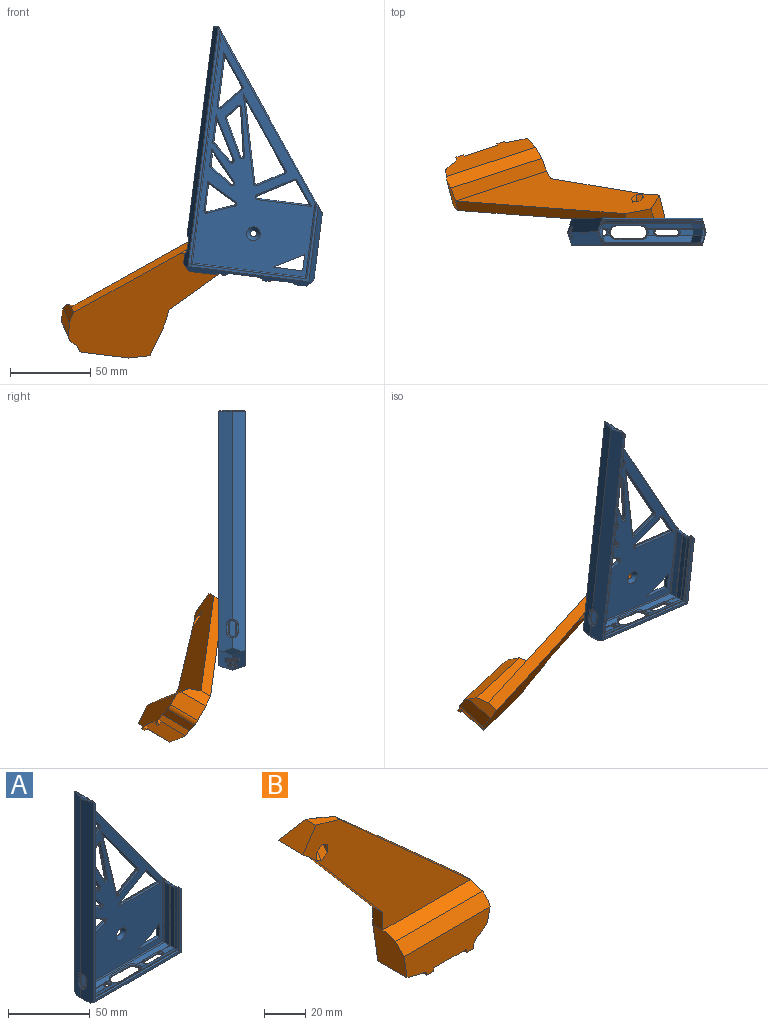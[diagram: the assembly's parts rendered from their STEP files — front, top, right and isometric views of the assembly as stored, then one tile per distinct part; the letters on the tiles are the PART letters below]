
ASSEMBLY  parts=2 mates=1
PART A: 277 faces, bbox 82x17x153.9 mm
  f0: plane 148.63x75.45mm, normal (0,1,0), area 4934.7mm2, adj f16,f37,f50,f70,f81,f82,f83,f110
  f1: cylinder r=0.8mm len=18.94mm, axis (1,0,0), area 5.1mm2, adj f33,f35,f47,f167
  f2: cylinder r=0.8mm len=5.41mm, axis (1,0,0), area 1.4mm2, adj f9,f35,f130,f158
  f3: cylinder r=0.8mm len=5.41mm, axis (1,0,0), area 1.4mm2, adj f9,f31,f134,f154
  f4: cylinder r=0.8mm len=2.64mm, axis (1,0,0), area 0.6mm2, adj f8,f31,f133,f164
  f5: plane 144.41x71.88mm, normal (0,-1,0), area 4754.3mm2, adj f17,f36,f49,f65,f81,f82,f83,f113
  f6: plane 13.8x13.8mm, normal (0,1,0), area 137mm2, adj f64,f69
  f7: cylinder r=0.8mm len=9.41mm, axis (1,0,0), area 2.5mm2, adj f10,f21,f31,f153
  f8: plane 3.72x1.63mm, normal (0,0,1), area 3.2mm2, adj f4,f34,f131,f162
  f9: plane 4.48x3.72mm, normal (0,0,1), area 13.9mm2, adj f2,f3,f132,f156
  f10: plane 8.76x3.72mm, normal (0,0,1), area 30.8mm2, adj f7,f11,f20,f155
  f11: cylinder r=0.8mm len=9.41mm, axis (1,0,0), area 2.5mm2, adj f10,f19,f35,f157
  f12: cylinder r=0.8mm len=132.11mm, axis (0,0,-1), area 36.6mm2, adj f13,f44,f99,f145
  f13: plane 131.79x3.73mm, normal (1,0,0), area 488.7mm2, adj f12,f14,f15,f99,f107,f143
  f14: cylinder r=0.8mm len=132.11mm, axis (0,0,-1), area 36.6mm2, adj f13,f48,f107,f141
  f15: plane 11.74x2.24mm, normal (0,0,1), area 11.7mm2, adj f13,f71,f73,f99,f100,f106,f107,f108
  f16: plane 47.9x8.81mm, normal (0.94,0.34,0), area 412.5mm2, adj f0,f26,f37,f74,f110,f112
  f17: cylinder r=0.8mm len=47.24mm, axis (0,0,1), area 44.9mm2, adj f5,f18,f36,f115
  f18: plane 46.45x3.49mm, normal (-0.94,-0.34,0), area 166.9mm2, adj f17,f19,f35,f117
  f19: cylinder r=0.8mm len=44.78mm, axis (0,0,1), area 12.4mm2, adj f11,f18,f20,f119
  f20: plane 44.65x3.72mm, normal (-1,0,0), area 166.1mm2, adj f10,f19,f21,f121
  f21: cylinder r=0.8mm len=44.78mm, axis (0,0,1), area 12.4mm2, adj f7,f20,f22,f123
  f22: plane 46.71x4.02mm, normal (-0.94,0.34,0), area 192.3mm2, adj f21,f31,f43,f125
  f23: cylinder r=0.8mm len=46.36mm, axis (0,0,1), area 57.8mm2, adj f24,f30,f43,f122
  f24: plane 45.56x0.4mm, normal (-1,0,0), area 18.2mm2, adj f23,f25,f29,f120
  f25: cylinder r=0.8mm len=46.36mm, axis (0,0,1), area 57.8mm2, adj f24,f28,f39,f118
  f26: plane 47.65x8.31mm, normal (0.94,-0.34,0), area 387.6mm2, adj f16,f27,f39,f74,f114,f116
  f27: plane 77.46x8.15mm, normal (0,-0.34,-0.94), area 469.6mm2, adj f26,f37,f38,f39,f72,f74,f172,f174
  f28: cylinder r=0.8mm len=72.6mm, axis (1,0,0), area 90.2mm2, adj f25,f29,f39,f40
  f29: plane 71x0.4mm, normal (0,0,1), area 28.4mm2, adj f24,f28,f30,f41
  f30: cylinder r=0.8mm len=72.6mm, axis (1,0,0), area 90.2mm2, adj f23,f29,f42,f43
  f31: plane 75.9x4.02mm, normal (0,0.34,0.94), area 258.9mm2, adj f3,f4,f7,f22,f32,f43,f44,f135
  f32: cylinder r=0.8mm len=18.94mm, axis (1,0,0), area 5.1mm2, adj f31,f33,f45,f168
  f33: plane 18.21x3.72mm, normal (0,0,1), area 65.8mm2, adj f1,f32,f46,f169
  f34: cylinder r=0.8mm len=2.64mm, axis (1,0,0), area 0.6mm2, adj f8,f35,f129,f163
  f35: plane 75.9x3.49mm, normal (0,-0.34,0.94), area 217.8mm2, adj f1,f2,f11,f18,f34,f36,f48,f126
  f36: cylinder r=0.8mm len=73.38mm, axis (1,0,0), area 71.1mm2, adj f5,f17,f35,f49
  f37: plane 77.46x8.65mm, normal (0,0.34,-0.94), area 509.8mm2, adj f0,f16,f27,f50,f72,f74,f170,f171
  f38: plane 150.44x8.16mm, normal (-0.94,-0.34,0), area 1256.9mm2, adj f27,f39,f50,f72,f105,f106,f184,f186
  f39: plane 149.05x75.81mm, normal (0,-1,0), area 428.9mm2, adj f25,f26,f27,f28,f38,f40,f105,f116
  f40: cylinder r=0.8mm len=145.26mm, axis (0,0,-1), area 182mm2, adj f28,f39,f41,f104
  f41: plane 144.46x0.4mm, normal (1,0,0), area 57.8mm2, adj f29,f40,f42,f103
  f42: cylinder r=0.8mm len=145.26mm, axis (0,0,-1), area 182mm2, adj f30,f41,f43,f102
  f43: plane 145.82x73.38mm, normal (0,1,0), area 53mm2, adj f22,f23,f30,f31,f42,f44,f101,f124
  f44: plane 150.36x4.46mm, normal (0.94,0.34,0), area 626.7mm2, adj f12,f31,f43,f45,f100,f101,f147,f148
  f45: cylinder r=0.8mm len=8.74mm, axis (0,0,-1), area 2.4mm2, adj f32,f44,f46,f146
  f46: plane 8.27x3.72mm, normal (1,0,0), area 29.3mm2, adj f33,f45,f47,f144
  f47: cylinder r=0.8mm len=8.74mm, axis (0,0,-1), area 2.4mm2, adj f1,f46,f48,f142
  f48: plane 150.19x3.49mm, normal (0.94,-0.34,0), area 544.1mm2, adj f14,f35,f47,f49,f109,f138,f139,f140
  f49: cylinder r=0.8mm len=147.21mm, axis (0,0,-1), area 142.8mm2, adj f5,f36,f48,f111
  f50: plane 150.44x8.66mm, normal (-0.94,0.34,0), area 1336.4mm2, adj f0,f37,f38,f72,f108,f110,f182,f183
  f51: plane 5x0.43mm, normal (0,-1,0), area 2.1mm2, adj f52,f54,f138,f183
  f52: cylinder r=2.5mm len=5mm, axis (1,0,0), area 4.5mm2, adj f51,f53,f139,f141,f143,f145,f147,f182
  f53: plane 5x0.43mm, normal (0,1,0), area 2.1mm2, adj f52,f54,f149,f186
  f54: cylinder r=2.5mm len=5mm, axis (1,0,0), area 4.5mm2, adj f51,f53,f140,f142,f144,f146,f148,f185
  f55: plane 11x0.43mm, normal (0,1,0), area 4.7mm2, adj f56,f58,f150,f180
  f56: cylinder r=2mm len=4mm, axis (0,0,1), area 3.9mm2, adj f55,f57,f151,f153,f155,f157,f159,f179
  f57: plane 11x0.43mm, normal (0,-1,0), area 4.7mm2, adj f56,f58,f161,f177
  f58: cylinder r=2mm len=4mm, axis (0,0,1), area 3.9mm2, adj f55,f57,f152,f154,f156,f158,f160,f176
  f59: plane 15x0.43mm, normal (0,1,0), area 6.4mm2, adj f60,f62,f137,f174
  f60: cylinder r=4mm len=8mm, axis (0,0,1), area 5.7mm2, adj f59,f61,f128,f130,f132,f134,f136,f173
  f61: plane 15x0.43mm, normal (0,-1,0), area 6.4mm2, adj f60,f62,f126,f171
  f62: cylinder r=4mm len=8mm, axis (0,0,1), area 5.7mm2, adj f59,f61,f127,f129,f131,f133,f135,f170
  f63: cylinder r=1.89mm len=3.78mm, axis (0,0,1), area 7.3mm2, adj f162,f163,f164,f165,f166,f167,f168,f169
  f64: cylinder r=2mm len=4mm, axis (0,1,0), area 2.5mm2, adj f6,f65
  f65: cone r=2mm half-angle=45deg, axis (0,-1,0), area 64.4mm2, adj f5,f64
  f66: cylinder r=7.4mm len=14.8mm, axis (0,1,0), area 46.5mm2, adj f68,f69
  f67: cylinder r=10.1mm len=20.2mm, axis (0,1,0), area 63.5mm2, adj f68,f70
  f68: plane 20.2x20.2mm, normal (0,1,0), area 148.4mm2, adj f66,f67
  f69: cone r=6.9mm half-angle=45deg, axis (0,-1,0), area 31.8mm2, adj f6,f66
  f70: cone r=10.1mm half-angle=45deg, axis (0,1,0), area 46mm2, adj f0,f67
  f71: plane 107.12x78.66mm, normal (0.81,0,0.59), area 134.7mm2, adj f15,f108,f109,f110,f111,f112,f113,f114
  f72: plane 11.74x4.24mm, normal (-0.71,0,-0.71), area 35.2mm2, adj f27,f37,f38,f50
  f73: plane 4.6x3.15mm, normal (0.81,0,0.59), area 6.6mm2, adj f15,f100,f101,f103,f105,f106
  f74: plane 11.74x4.24mm, normal (0.71,0,-0.71), area 35.2mm2, adj f16,f26,f27,f37
  f75: plane 31.09x0.9mm, normal (1,0,0), area 28mm2, adj f76,f265,f270,f274
  f76: plane 17.75x13.03mm, normal (-0.81,0,-0.59), area 19.8mm2, adj f75,f263,f267,f272
  f77: plane 12.86x11.59mm, normal (-0.74,0,0.67), area 15.6mm2, adj f266,f267,f270,f271
  f78: plane 16.84x0.9mm, normal (1,0,0), area 15.2mm2, adj f79,f252,f257,f262
  f79: plane 17.72x9.78mm, normal (-0.48,0,-0.88), area 18.2mm2, adj f78,f251,f256,f261
  f80: plane 16.54x6.36mm, normal (-0.36,0,0.93), area 15.9mm2, adj f253,f256,f257,f258
  f81: plane 10.14x2.5mm, normal (-1,0,0), area 25.3mm2, adj f0,f5,f82,f83
  f82: plane 18.35x2.5mm, normal (0,0,1), area 45.9mm2, adj f0,f5,f81,f83
  f83: plane 18.39x10.14mm, normal (0.48,0,-0.88), area 52.5mm2, adj f0,f5,f81,f82
  f84: plane 13.72x10.07mm, normal (-0.81,0,-0.59), area 15.3mm2, adj f85,f241,f246,f250
  f85: plane 32.4x0.9mm, normal (0,0,1), area 29.2mm2, adj f84,f239,f243,f248
  f86: plane 21.69x12.45mm, normal (0.5,0,-0.87), area 22.5mm2, adj f242,f243,f246,f247
  f87: plane 22.6x11.63mm, normal (0.89,0,0.46), area 22.9mm2, adj f226,f233,f234,f238
  f88: plane 6.86x6.17mm, normal (0.74,0,-0.67), area 8.3mm2, adj f225,f228,f232,f233
  f89: plane 29.46x5.46mm, normal (-0.98,0,-0.18), area 27mm2, adj f227,f228,f234,f235
  f90: plane 14.08x0.9mm, normal (1,0,0), area 12.7mm2, adj f91,f213,f218,f223
  f91: plane 23.83x13.13mm, normal (-0.88,0,-0.48), area 24.5mm2, adj f90,f212,f217,f222
  f92: plane 11.63x10.13mm, normal (0.66,0,0.75), area 13.9mm2, adj f214,f217,f218,f219
  f93: plane 8.38x0.9mm, normal (1,0,0), area 7.5mm2, adj f94,f201,f206,f211
  f94: plane 17.3x15.12mm, normal (-0.75,0,-0.66), area 20.7mm2, adj f93,f200,f205,f210
  f95: plane 13.72x9.45mm, normal (0.57,0,0.82), area 15mm2, adj f202,f205,f206,f207
  f96: plane 50.74x12.4mm, normal (0.97,0,0.24), area 47mm2, adj f97,f190,f195,f199
  f97: plane 40.81x29.96mm, normal (-0.81,0,-0.59), area 45.6mm2, adj f96,f188,f192,f197
  f98: plane 16.13x9.26mm, normal (-0.5,0,0.87), area 16.7mm2, adj f191,f192,f195,f196
  f99: bspline ~1.16x0.68mm, area 0.1mm2, adj f12,f13,f15,f100
  f100: cylinder r=0.8mm len=4.82mm, axis (0.31,-0.85,-0.42), area 2.9mm2, adj f15,f44,f73,f99,f101
  f101: cylinder r=0.8mm len=1.51mm, axis (0.59,0,-0.81), area 1.1mm2, adj f43,f44,f73,f100,f102
  f102: sphere r=0.8mm, area 0.6mm2, adj f42,f101,f103
  f103: cylinder r=0.8mm len=0.47mm, axis (0,-1,0), area 0.2mm2, adj f41,f73,f102,f104
  f104: sphere r=0.8mm, area 0.6mm2, adj f40,f103,f105
  f105: cylinder r=0.8mm len=3.41mm, axis (-0.59,0,0.81), area 4.1mm2, adj f38,f39,f73,f104,f106
  f106: cylinder r=0.8mm len=8.36mm, axis (-0.34,0.94,0), area 9.7mm2, adj f15,f38,f73,f105,f108
  f107: bspline ~1.16x0.68mm, area 0.1mm2, adj f13,f14,f15,f109
  f108: cylinder r=0.8mm len=8.79mm, axis (0.34,0.94,0), area 10mm2, adj f15,f50,f71,f106,f110
  f109: cylinder r=0.8mm len=3.76mm, axis (-0.31,-0.85,0.42), area 2.3mm2, adj f15,f48,f71,f107,f111
  f110: cylinder r=0.8mm len=104.16mm, axis (0.59,0,-0.81), area 160.4mm2, adj f0,f16,f50,f71,f108,f112
  f111: bspline ~2.52x1.5mm, area 2.3mm2, adj f49,f71,f109,f113
  f112: cylinder r=0.8mm len=8.64mm, axis (0.31,-0.85,-0.42), area 5.4mm2, adj f16,f71,f110,f114
  f113: cylinder r=0.8mm len=98.39mm, axis (-0.59,0,0.81), area 152.6mm2, adj f5,f71,f111,f115
  f114: cylinder r=0.8mm len=8.14mm, axis (-0.31,-0.85,0.42), area 5.1mm2, adj f26,f71,f112,f116
  f115: bspline ~2.65x2.24mm, area 3.7mm2, adj f17,f71,f113,f117
  f116: cylinder r=0.8mm len=2.66mm, axis (-0.59,0,0.81), area 2.7mm2, adj f26,f39,f71,f114,f118
  f117: cylinder r=0.8mm len=3.91mm, axis (-0.31,0.85,0.42), area 8mm2, adj f18,f71,f115,f119
  f118: sphere r=0.8mm, area 1.3mm2, adj f25,f116,f120
  f119: bspline ~1.52x0.9mm, area 0.5mm2, adj f19,f71,f117,f121
  f120: cylinder r=0.8mm len=1.45mm, axis (0,1,0), area 0.8mm2, adj f24,f71,f118,f122
  f121: cylinder r=0.8mm len=3.72mm, axis (0,1,0), area 7.5mm2, adj f20,f71,f119,f123
  f122: sphere r=0.8mm, area 1.1mm2, adj f23,f120,f124
  f123: bspline ~1.52x0.9mm, area 0.5mm2, adj f21,f71,f121,f125
  f124: cylinder r=0.8mm len=1.51mm, axis (0.59,0,-0.81), area 1.3mm2, adj f43,f71,f122,f125
  f125: cylinder r=0.8mm len=4.96mm, axis (0.31,0.85,-0.42), area 9.7mm2, adj f22,f43,f71,f123,f124
  f126: cylinder r=0.8mm len=15mm, axis (1,0,0), area 14.7mm2, adj f35,f61,f127,f128
  f127: bspline ~4.15x2.57mm, area 4.8mm2, adj f35,f62,f126,f129
  f128: bspline ~4.15x2.57mm, area 4.8mm2, adj f35,f60,f126,f130
  f129: bspline ~1.32x1.09mm, area 0.5mm2, adj f34,f62,f127,f131
  f130: bspline ~1.22x0.96mm, area 0.5mm2, adj f2,f60,f128,f132
  f131: torus R=4.8mm, axis (0,0,1), area 4.3mm2, adj f8,f62,f129,f133
  f132: torus R=4.8mm, axis (0,0,1), area 4.3mm2, adj f9,f60,f130,f134
  f133: bspline ~1.22x0.96mm, area 0.5mm2, adj f4,f62,f131,f135
  f134: bspline ~1.32x1.09mm, area 0.5mm2, adj f3,f60,f132,f136
  f135: bspline ~4.15x2.57mm, area 4.8mm2, adj f31,f62,f133,f137
  f136: bspline ~4.15x2.57mm, area 4.8mm2, adj f31,f60,f134,f137
  f137: cylinder r=0.8mm len=15mm, axis (-1,0,0), area 14.7mm2, adj f31,f59,f135,f136
  f138: cylinder r=0.8mm len=5mm, axis (0,0,-1), area 4.9mm2, adj f48,f51,f139,f140
  f139: bspline ~2.44x1.46mm, area 2.2mm2, adj f48,f52,f138,f141
  f140: bspline ~2.44x1.46mm, area 2.2mm2, adj f48,f54,f138,f142
  f141: bspline ~1.6x1.17mm, area 0.6mm2, adj f14,f52,f139,f143
  f142: bspline ~1.46x0.99mm, area 0.6mm2, adj f47,f54,f140,f144
  f143: torus R=3.3mm, axis (1,0,0), area 4.2mm2, adj f13,f52,f141,f145
  f144: torus R=3.3mm, axis (1,0,0), area 4.2mm2, adj f46,f54,f142,f146
  f145: bspline ~1.6x1.17mm, area 0.6mm2, adj f12,f52,f143,f147
  f146: bspline ~1.6x1.17mm, area 0.6mm2, adj f45,f54,f144,f148
  f147: bspline ~2.44x1.46mm, area 2.2mm2, adj f44,f52,f145,f149
  f148: bspline ~2.44x1.46mm, area 2.2mm2, adj f44,f54,f146,f149
  f149: cylinder r=0.8mm len=5mm, axis (0,0,1), area 4.9mm2, adj f44,f53,f147,f148
  f150: cylinder r=0.8mm len=11mm, axis (-1,0,0), area 10.8mm2, adj f31,f55,f151,f152
  f151: bspline ~1.44x0.9mm, area 1.3mm2, adj f31,f56,f150,f153
  f152: bspline ~1.44x0.9mm, area 1.3mm2, adj f31,f58,f150,f154
  f153: bspline ~1.61x1.12mm, area 0.7mm2, adj f7,f56,f151,f155
  f154: bspline ~1.57x1.11mm, area 0.7mm2, adj f3,f58,f152,f156
  f155: torus R=2.8mm, axis (0,0,1), area 4.2mm2, adj f10,f56,f153,f157
  f156: torus R=2.8mm, axis (0,0,1), area 4.2mm2, adj f9,f58,f154,f158
  f157: bspline ~1.4x0.95mm, area 0.7mm2, adj f11,f56,f155,f159
  f158: bspline ~1.61x1.12mm, area 0.7mm2, adj f2,f58,f156,f160
  f159: bspline ~1.44x0.9mm, area 1.3mm2, adj f35,f56,f157,f161
  f160: bspline ~1.44x0.9mm, area 1.3mm2, adj f35,f58,f158,f161
  f161: cylinder r=0.8mm len=11mm, axis (-1,0,0), area 10.8mm2, adj f35,f57,f159,f160
  f162: torus R=2.69mm, axis (0,0,1), area 4.2mm2, adj f8,f63,f163,f164
  f163: bspline ~1.41x1.06mm, area 0.7mm2, adj f34,f63,f162,f165
  f164: bspline ~1.61x1.11mm, area 0.7mm2, adj f4,f63,f162,f166
  f165: bspline ~2.42x0.86mm, area 2.1mm2, adj f35,f63,f163,f167
  f166: bspline ~2.42x0.86mm, area 2.1mm2, adj f31,f63,f164,f168
  f167: bspline ~1.61x1.11mm, area 0.7mm2, adj f1,f63,f165,f169
  f168: bspline ~1.41x1.06mm, area 0.7mm2, adj f32,f63,f166,f169
  f169: torus R=2.69mm, axis (0,0,1), area 4.2mm2, adj f33,f63,f167,f168
  f170: bspline ~5.3x4.8mm, area 10.1mm2, adj f37,f62,f171,f172
  f171: cylinder r=0.8mm len=15mm, axis (-1,0,0), area 23mm2, adj f37,f61,f170,f173
  f172: bspline ~5.3x4.8mm, area 10.1mm2, adj f27,f62,f170,f174
  f173: bspline ~5.3x4.8mm, area 10.1mm2, adj f37,f60,f171,f175
  f174: cylinder r=0.8mm len=15mm, axis (1,0,0), area 23mm2, adj f27,f59,f172,f175
  f175: bspline ~5.3x4.8mm, area 10.1mm2, adj f27,f60,f173,f174
  f176: bspline ~3.27x2.8mm, area 5.5mm2, adj f37,f58,f177,f178
  f177: cylinder r=0.8mm len=11mm, axis (-1,0,0), area 16.9mm2, adj f37,f57,f176,f179
  f178: bspline ~3.27x2.8mm, area 5.5mm2, adj f27,f58,f176,f180
  f179: bspline ~3.27x2.8mm, area 5.5mm2, adj f37,f56,f177,f181
  f180: cylinder r=0.8mm len=11mm, axis (1,0,0), area 16.9mm2, adj f27,f55,f178,f181
  f181: bspline ~3.27x2.8mm, area 5.5mm2, adj f27,f56,f179,f180
  f182: bspline ~4.01x3.3mm, area 6.7mm2, adj f50,f52,f183,f184
  f183: cylinder r=0.8mm len=5mm, axis (0,0,1), area 7.7mm2, adj f50,f51,f182,f185
  f184: bspline ~4.01x3.3mm, area 6.7mm2, adj f38,f52,f182,f186
  f185: bspline ~4.01x3.3mm, area 6.7mm2, adj f50,f54,f183,f187
  f186: cylinder r=0.8mm len=5mm, axis (0,0,-1), area 7.7mm2, adj f38,f53,f184,f187
  f187: bspline ~4.01x3.3mm, area 6.7mm2, adj f38,f54,f185,f186
  f188: cylinder r=0.8mm len=44.52mm, axis (-0.59,0,0.81), area 65.5mm2, adj f0,f97,f189,f190
  f189: torus R=1.6mm, axis (0,1,0), area 2.3mm2, adj f0,f188,f191,f192
  f190: cylinder r=0.8mm len=54.82mm, axis (0.24,0,-0.97), area 67.5mm2, adj f0,f96,f188,f193
  f191: cylinder r=0.8mm len=16.53mm, axis (0.87,0,0.5), area 23.4mm2, adj f0,f98,f189,f193
  f192: cylinder r=0.8mm len=1.17mm, axis (0,-1,0), area 1.2mm2, adj f97,f98,f189,f194
  f193: torus R=1.6mm, axis (0,1,0), area 2.5mm2, adj f0,f190,f191,f195
  f194: torus R=1.6mm, axis (0,-1,0), area 2.3mm2, adj f5,f192,f196,f197
  f195: cylinder r=0.8mm len=1.18mm, axis (0,-1,0), area 1.3mm2, adj f96,f98,f193,f198
  f196: cylinder r=0.8mm len=16.53mm, axis (-0.87,0,-0.5), area 23.4mm2, adj f5,f98,f194,f198
  f197: cylinder r=0.8mm len=44.52mm, axis (0.59,0,-0.81), area 65.5mm2, adj f5,f97,f194,f199
  f198: torus R=1.6mm, axis (0,-1,0), area 2.5mm2, adj f5,f195,f196,f199
  f199: cylinder r=0.8mm len=54.82mm, axis (-0.24,0,0.97), area 67.5mm2, adj f5,f96,f197,f198
  f200: cylinder r=0.8mm len=19.43mm, axis (-0.66,0,0.75), area 30.2mm2, adj f0,f94,f201,f203
  f201: cylinder r=0.8mm len=10.51mm, axis (0,0,-1), area 11.9mm2, adj f0,f93,f200,f204
  f202: cylinder r=0.8mm len=14.17mm, axis (0.82,0,-0.57), area 20.9mm2, adj f0,f95,f203,f204
  f203: torus R=1.6mm, axis (0,1,0), area 4mm2, adj f0,f200,f202,f205
  f204: torus R=1.6mm, axis (0,1,0), area 1.3mm2, adj f0,f201,f202,f206
  f205: cylinder r=0.8mm len=1.33mm, axis (0,-1,0), area 2.1mm2, adj f94,f95,f203,f208
  f206: cylinder r=0.8mm len=0.9mm, axis (0,-1,0), area 0.7mm2, adj f93,f95,f204,f209
  f207: cylinder r=0.8mm len=14.17mm, axis (-0.82,0,0.57), area 20.9mm2, adj f5,f95,f208,f209
  f208: torus R=1.6mm, axis (0,-1,0), area 4mm2, adj f5,f205,f207,f210
  f209: torus R=1.6mm, axis (0,-1,0), area 1.3mm2, adj f5,f206,f207,f211
  f210: cylinder r=0.8mm len=19.43mm, axis (0.66,0,-0.75), area 30.2mm2, adj f5,f94,f208,f211
  f211: cylinder r=0.8mm len=10.51mm, axis (0,0,1), area 11.9mm2, adj f5,f93,f209,f210
  f212: cylinder r=0.8mm len=26.94mm, axis (-0.48,0,0.88), area 35.6mm2, adj f0,f91,f213,f215
  f213: cylinder r=0.8mm len=17.19mm, axis (0,0,-1), area 19.1mm2, adj f0,f90,f212,f216
  f214: cylinder r=0.8mm len=12.16mm, axis (0.75,0,-0.66), area 19.4mm2, adj f0,f92,f215,f216
  f215: torus R=1.6mm, axis (0,1,0), area 3.8mm2, adj f0,f212,f214,f217
  f216: torus R=1.6mm, axis (0,1,0), area 1.2mm2, adj f0,f213,f214,f218
  f217: cylinder r=0.8mm len=1.33mm, axis (0,-1,0), area 2mm2, adj f91,f92,f215,f220
  f218: cylinder r=0.8mm len=0.9mm, axis (0,-1,0), area 0.6mm2, adj f90,f92,f216,f221
  f219: cylinder r=0.8mm len=12.16mm, axis (-0.75,0,0.66), area 19.4mm2, adj f5,f92,f220,f221
  f220: torus R=1.6mm, axis (0,-1,0), area 3.8mm2, adj f5,f217,f219,f222
  f221: torus R=1.6mm, axis (0,-1,0), area 1.2mm2, adj f5,f218,f219,f223
  f222: cylinder r=0.8mm len=26.94mm, axis (0.48,0,-0.88), area 35.6mm2, adj f5,f91,f220,f223
  f223: cylinder r=0.8mm len=17.19mm, axis (0,0,1), area 19.1mm2, adj f5,f90,f221,f222
  f224: torus R=1.6mm, axis (0,1,0), area 3mm2, adj f0,f225,f227,f228
  f225: cylinder r=0.8mm len=7.39mm, axis (-0.67,0,-0.74), area 11.6mm2, adj f0,f88,f224,f229
  f226: cylinder r=0.8mm len=22.97mm, axis (0.46,0,-0.89), area 31.9mm2, adj f0,f87,f229,f230
  f227: cylinder r=0.8mm len=29.6mm, axis (-0.18,0,0.98), area 37.6mm2, adj f0,f89,f224,f230
  f228: cylinder r=0.8mm len=1.38mm, axis (0,-1,0), area 1.6mm2, adj f88,f89,f224,f231
  f229: torus R=1.6mm, axis (0,1,0), area 1.7mm2, adj f0,f225,f226,f233
  f230: torus R=1.6mm, axis (0,1,0), area 3.9mm2, adj f0,f226,f227,f234
  f231: torus R=1.6mm, axis (0,-1,0), area 3mm2, adj f5,f228,f232,f235
  f232: cylinder r=0.8mm len=7.39mm, axis (0.67,0,0.74), area 11.6mm2, adj f5,f88,f231,f236
  f233: cylinder r=0.8mm len=0.9mm, axis (0,-1,0), area 0.9mm2, adj f87,f88,f229,f236
  f234: cylinder r=0.8mm len=1.51mm, axis (0,-1,0), area 2.1mm2, adj f87,f89,f230,f237
  f235: cylinder r=0.8mm len=29.6mm, axis (0.18,0,-0.98), area 37.6mm2, adj f5,f89,f231,f237
  f236: torus R=1.6mm, axis (0,-1,0), area 1.7mm2, adj f5,f232,f233,f238
  f237: torus R=1.6mm, axis (0,-1,0), area 3.9mm2, adj f5,f234,f235,f238
  f238: cylinder r=0.8mm len=22.97mm, axis (-0.46,0,0.89), area 31.9mm2, adj f5,f87,f236,f237
  f239: cylinder r=0.8mm len=33.98mm, axis (1,0,0), area 41.7mm2, adj f0,f85,f240,f241
  f240: torus R=1.6mm, axis (0,1,0), area 3.6mm2, adj f0,f239,f242,f243
  f241: cylinder r=0.8mm len=15.47mm, axis (-0.59,0,0.81), area 22.4mm2, adj f0,f84,f239,f244
  f242: cylinder r=0.8mm len=22.08mm, axis (-0.87,0,-0.5), area 31.4mm2, adj f0,f86,f240,f244
  f243: cylinder r=0.8mm len=1.49mm, axis (0,-1,0), area 1.9mm2, adj f85,f86,f240,f245
  f244: torus R=1.6mm, axis (0,1,0), area 2mm2, adj f0,f241,f242,f246
  f245: torus R=1.6mm, axis (0,-1,0), area 3.6mm2, adj f5,f243,f247,f248
  f246: cylinder r=0.8mm len=1.04mm, axis (0,-1,0), area 1.1mm2, adj f84,f86,f244,f249
  f247: cylinder r=0.8mm len=22.08mm, axis (0.87,0,0.5), area 31.4mm2, adj f5,f86,f245,f249
  f248: cylinder r=0.8mm len=33.98mm, axis (-1,0,0), area 41.7mm2, adj f5,f85,f245,f250
  f249: torus R=1.6mm, axis (0,-1,0), area 2mm2, adj f5,f246,f247,f250
  f250: cylinder r=0.8mm len=15.47mm, axis (0.59,0,-0.81), area 22.4mm2, adj f5,f84,f248,f249
  f251: cylinder r=0.8mm len=19.3mm, axis (-0.88,0,0.48), area 26.3mm2, adj f0,f79,f252,f254
  f252: cylinder r=0.8mm len=18.19mm, axis (0,0,-1), area 22mm2, adj f0,f78,f251,f255
  f253: cylinder r=0.8mm len=16.82mm, axis (0.93,0,0.36), area 22.3mm2, adj f0,f80,f254,f255
  f254: torus R=1.6mm, axis (0,1,0), area 3.1mm2, adj f0,f251,f253,f256
  f255: torus R=1.6mm, axis (0,1,0), area 2.7mm2, adj f0,f252,f253,f257
  f256: cylinder r=0.8mm len=1.45mm, axis (0,-1,0), area 1.6mm2, adj f79,f80,f254,f259
  f257: cylinder r=0.8mm len=1.09mm, axis (0,-1,0), area 1.4mm2, adj f78,f80,f255,f260
  f258: cylinder r=0.8mm len=16.82mm, axis (-0.93,0,-0.36), area 22.3mm2, adj f5,f80,f259,f260
  f259: torus R=1.6mm, axis (0,-1,0), area 3.1mm2, adj f5,f256,f258,f261
  f260: torus R=1.6mm, axis (0,-1,0), area 2.7mm2, adj f5,f257,f258,f262
  f261: cylinder r=0.8mm len=19.3mm, axis (0.88,0,-0.48), area 26.3mm2, adj f5,f79,f259,f262
  f262: cylinder r=0.8mm len=18.19mm, axis (0,0,1), area 22mm2, adj f5,f78,f260,f261
  f263: cylinder r=0.8mm len=20.19mm, axis (-0.59,0,0.81), area 29.2mm2, adj f0,f76,f264,f265
  f264: torus R=1.6mm, axis (0,1,0), area 1.9mm2, adj f0,f263,f266,f267
  f265: cylinder r=0.8mm len=33.53mm, axis (0,0,-1), area 40.6mm2, adj f0,f75,f263,f268
  f266: cylinder r=0.8mm len=13.4mm, axis (0.67,0,0.74), area 21.8mm2, adj f0,f77,f264,f268
  f267: cylinder r=0.8mm len=1.01mm, axis (0,-1,0), area 1mm2, adj f76,f77,f264,f269
  f268: torus R=1.6mm, axis (0,1,0), area 3.3mm2, adj f0,f265,f266,f270
  f269: torus R=1.6mm, axis (0,-1,0), area 1.9mm2, adj f5,f267,f271,f272
  f270: cylinder r=0.8mm len=1.39mm, axis (0,-1,0), area 1.7mm2, adj f75,f77,f268,f273
  f271: cylinder r=0.8mm len=13.4mm, axis (-0.67,0,-0.74), area 21.8mm2, adj f5,f77,f269,f273
  f272: cylinder r=0.8mm len=20.19mm, axis (0.59,0,-0.81), area 29.2mm2, adj f5,f76,f269,f274
  f273: torus R=1.6mm, axis (0,-1,0), area 3.3mm2, adj f5,f270,f271,f274
  f274: cylinder r=0.8mm len=33.53mm, axis (0,0,1), area 40.6mm2, adj f5,f75,f272,f273
  f275: bspline ~5.38x3.16mm, area 10.5mm2, adj f37,f63,f276
  f276: bspline ~5.38x3.16mm, area 10.5mm2, adj f27,f63,f275
PART B: 43 faces, bbox 116x31x114.3 mm
  f0: plane 107.46x91.62mm, normal (0,1,0), area 4054.8mm2, adj f4,f8,f12,f13,f14,f15,f16,f17
  f1: plane 114.93x85.29mm, normal (0,-1,0), area 3291.2mm2, adj f19,f21,f22,f24,f26,f27,f35,f36
  f2: plane 58.96x19mm, normal (0,-1,0), area 908.7mm2, adj f4,f5,f6,f7,f8,f9,f10,f11
  f3: plane 5x2mm, normal (0,1,0), area 10mm2, adj f5,f6,f7,f8
  f4: plane 20x13.5mm, normal (-0.25,0,-0.97), area 278.9mm2, adj f0,f2,f5,f8,f17
  f5: plane 2x2mm, normal (-1,0,0), area 4mm2, adj f2,f3,f4,f6
  f6: plane 5x2mm, normal (0,0,-1), area 10mm2, adj f2,f3,f5,f7
  f7: plane 2x2mm, normal (1,0,0), area 4mm2, adj f2,f3,f6,f8
  f8: plane 32x20mm, normal (0,0,-1), area 620mm2, adj f0,f2,f3,f4,f7,f9,f12,f18
  f9: plane 2x2mm, normal (-1,0,0), area 4mm2, adj f2,f8,f10,f18
  f10: plane 5x2mm, normal (0,0,-1), area 10mm2, adj f2,f9,f11,f18
  f11: plane 2x2mm, normal (1,0,0), area 4mm2, adj f2,f10,f12,f18
  f12: plane 20x3.46mm, normal (0.83,0,-0.55), area 83mm2, adj f0,f2,f8,f11,f13
  f13: plane 20x5.2mm, normal (0.51,0,-0.86), area 121mm2, adj f0,f2,f12,f14
  f14: cylinder r=5mm len=20mm, axis (0,1,0), area 81.6mm2, adj f0,f2,f13,f15
  f15: plane 20x10.04mm, normal (0.98,0,-0.22), area 202.8mm2, adj f0,f2,f14,f16,f20
  f16: plane 18.01x7.21mm, normal (0.99,0,0.15), area 103.6mm2, adj f0,f15,f19,f20,f22
  f17: plane 23.5x20mm, normal (-0.99,0,-0.15), area 430.2mm2, adj f0,f2,f4,f19,f20,f26
  f18: plane 5x2mm, normal (0,1,0), area 10mm2, adj f8,f9,f10,f11
  f19: plane 60.45x8mm, normal (0,-0.35,0.94), area 512.6mm2, adj f1,f16,f17,f20
  f20: plane 60.63x7mm, normal (0,-0.81,0.58), area 514.3mm2, adj f2,f15,f16,f17,f19
  f21: plane 16.02x7mm, normal (0.27,0,0.96), area 87.1mm2, adj f1,f22,f25,f42
  f22: plane 90x80.8mm, normal (0.67,0,0.74), area 767mm2, adj f0,f1,f16,f21,f25
  f23: plane 50x14mm, normal (-0.27,0,-0.96), area 286.5mm2, adj f0,f24,f25
  f24: plane 18.04x8.55mm, normal (-0.67,0,-0.74), area 201.3mm2, adj f1,f23,f25,f27,f42
  f25: plane 58.48x34.66mm, normal (0.31,0.84,0.44), area 606.4mm2, adj f21,f22,f23,f24,f29,f42
  f26: plane 10.42x7mm, normal (-1,0,0), area 73mm2, adj f0,f1,f17,f27
  f27: plane 54.2x46.38mm, normal (-0.76,0,-0.65), area 499.3mm2, adj f0,f1,f24,f26
  f28: cylinder r=7.5mm len=14.57mm, axis (-0.31,-0.84,-0.44), area 47.1mm2, adj f31,f32
  f29: cylinder r=10mm len=19.33mm, axis (-0.31,-0.84,-0.44), area 62.8mm2, adj f25,f33
  f30: plane 18.07x17.03mm, normal (0.31,0.84,0.44), area 82.5mm2, adj f32,f33
  f31: plane 14.26x13.45mm, normal (0.31,0.84,0.44), area 164.1mm2, adj f28,f34
  f32: cone r=7.5mm half-angle=45deg, axis (0.31,0.84,0.44), area 34.4mm2, adj f28,f30
  f33: cone r=9.5mm half-angle=45deg, axis (-0.31,-0.84,-0.44), area 43.3mm2, adj f29,f30
  f34: cylinder r=2mm len=4.92mm, axis (0.31,0.84,0.44), area 37.7mm2, adj f31,f41
  f35: plane 10.17x7.34mm, normal (0.41,-0.54,0.74), area 49.1mm2, adj f1,f36,f40,f41
  f36: plane 10.17x9.03mm, normal (0.95,-0.31,-0.07), area 45.2mm2, adj f1,f35,f37,f41
  f37: plane 8.36x6.28mm, normal (0.54,0.23,-0.81), area 35.8mm2, adj f1,f36,f38,f41
  f38: plane 6.35x5.86mm, normal (-0.41,0.54,-0.74), area 30.5mm2, adj f1,f37,f39,f41
  f39: plane 7.96x7.86mm, normal (-0.95,0.31,0.07), area 34.4mm2, adj f1,f38,f40,f41
  f40: plane 9.97x6.88mm, normal (-0.54,-0.23,0.81), area 43.7mm2, adj f1,f35,f39,f41
  f41: plane 7.33x7.05mm, normal (-0.31,-0.84,-0.44), area 31.1mm2, adj f34,f35,f36,f37,f38,f39,f40
  f42: plane 17.15x13.05mm, normal (-0.82,0.01,0.57), area 190.4mm2, adj f1,f21,f24,f25
PLACE A rot(axis=(0,1,0),7.2deg) t=(-248.92,34.02,-18.33)mm
PLACE B rot(axis=(-0.1,0.25,-0.96),164.2deg) t=(-268.63,87.02,-46.38)mm
MATE fastened B.f34 <-> A.f64  axis (0,-1,0) through (-209.71,48.32,0.79)mm
